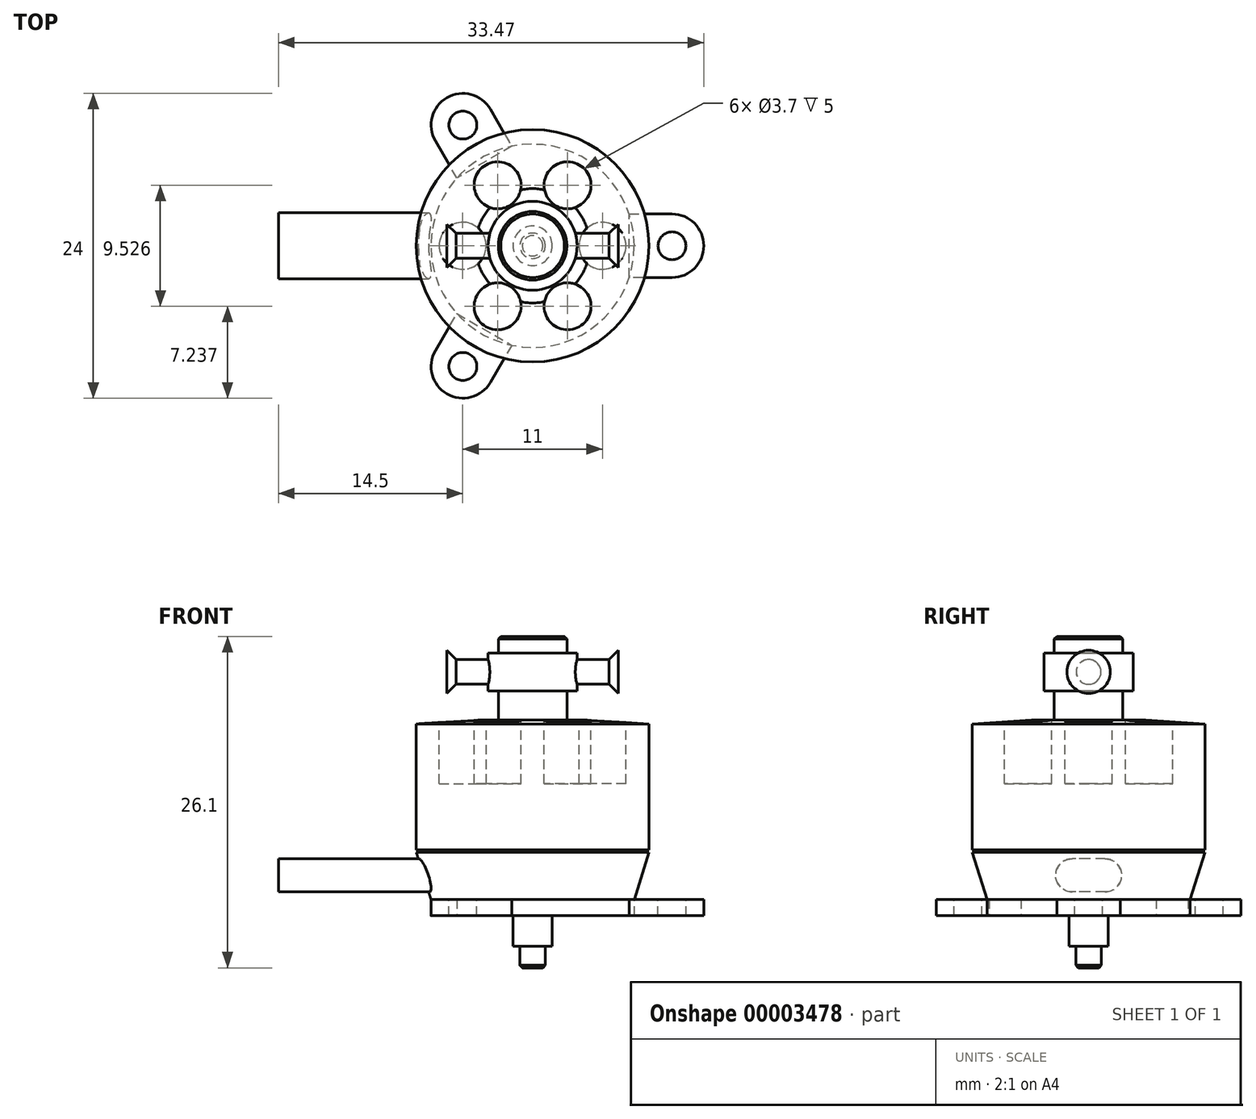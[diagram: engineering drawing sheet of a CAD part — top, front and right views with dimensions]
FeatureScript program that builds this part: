
annotation { "Feature Type Name" : "Feature", "Feature Type Description" : "" }
export const myFeature = defineFeature(function(context is Context, id is Id, definition is map)
    precondition{}
    {
        {
            var Q0;
            Q0=qCreatedBy(makeId("Top.planeOp"),FACE);
            var sketch = newSketch(context, id + "F0", { "sketchPlane" : qUnion([Q0])});
            skCircle(sketch, "E0", {"center": v(0, 0) * mm, "radius": 9.15 * mm});
            skSolve(sketch);
        }
        {
            var Q0;
            Q0=makeQuery(id+"F0.imprint","IMPRINT",FACE,{"disambiguationData":[TD([[makeQuery(id+"F0.imprint","IMPRINT",EDGE,{"derivedFrom":sQuery(id+"F0.wireOp",EDGE,"E0")}),1.0]])]});
            extrude(context, id + "F1", {"entities" : qUnion([Q0]), "depth" : 10.2 * mm});
        }
        {
            var Q0;
            Q0=makeQuery(id+"F1.opExtrude","CAP_FACE",FACE,{"disambiguationData":[OSD([sQuery(id+"F0.wireOp",EDGE,"E0")])],"isStart":true});
            var sketch = newSketch(context, id + "F2", { "sketchPlane" : qUnion([Q0])});
            skCircle(sketch, "E1", {"center": v(0, 0) * mm, "radius": 8 * mm});
            skSolve(sketch);
        }
        {
            var Q0;
            Q0=makeQuery(id+"F2.imprint","IMPRINT",FACE,{"disambiguationData":[TD([[makeQuery(id+"F2.imprint","IMPRINT",EDGE,{"derivedFrom":sQuery(id+"F2.wireOp",EDGE,"E1")}),1.0]])]});
            extrude(context, id + "F3", {"entities" : qUnion([Q0]), "operationType" : NewBodyOperationType.ADD, "depth" : 0.2 * mm});
        }
        {
            var Q0;
            Q0=makeQuery(id+"F3.opExtrude","CAP_FACE",FACE,{"disambiguationData":[OSD([sQuery(id+"F2.wireOp",EDGE,"E1")])],"isStart":false});
            var sketch = newSketch(context, id + "F4", { "sketchPlane" : qUnion([Q0])});
            skCircle(sketch, "E2", {"center": v(0, 0) * mm, "radius": 9.15 * mm});
            skSolve(sketch);
        }
        {
            var Q0;
            {var subQ0=makeQuery(id+"F4.imprint","IMPRINT",EDGE,{"derivedFrom":makeQuery(id+"F3.opExtrude","CAP_EDGE",EDGE,{"disambiguationData":[OSD([sQuery(id+"F2.wireOp",EDGE,"E1")])],"isStart":false})});Q0=qUnion([makeQuery(id+"F4.imprint","IMPRINT",FACE,{"disambiguationData":[TD([[makeQuery(id+"F4.imprint","IMPRINT",EDGE,{"derivedFrom":sQuery(id+"F4.wireOp",EDGE,"E2")}),1.0]])]}),makeQuery(id+"F4.imprint","IMPRINT",FACE,{"disambiguationData":[TD([[subQ0,1.0]])]})]);}
            extrude(context, id + "F5", {"entities" : qUnion([Q0]), "depth" : 3.7 * mm});
        }
        {
            var Q0;
            Q0=makeQuery(id+"F5.opExtrude","CAP_EDGE",EDGE,{"disambiguationData":[OSD([sQuery(id+"F4.wireOp",EDGE,"E2")])],"isStart":false});
            chamfer(context, id + "F6", {"entities" : qUnion([Q0]), "chamferType" : ChamferType.TWO_OFFSETS, "width1" : 1.15 * mm, "oppositeDirection" : false, "width2" : 3.7 * mm, "tangentPropagation" : true});
        }
        {
            var Q0;
            Q0=makeQuery(id+"F5.opExtrude","CAP_FACE",FACE,{"disambiguationData":[OSD([sQuery(id+"F4.wireOp",EDGE,"E2")])],"isStart":false});
            var sketch = newSketch(context, id + "F7", { "sketchPlane" : qUnion([Q0])});
            skCircle(sketch, "E3", {"center": v(0, 0) * mm, "radius": 8 * mm});
            skSolve(sketch);
        }
        {
            var Q0;
            Q0=makeQuery(id+"F7.imprint","IMPRINT",FACE,{"disambiguationData":[TD([[makeQuery(id+"F7.imprint","IMPRINT",EDGE,{"derivedFrom":sQuery(id+"F7.wireOp",EDGE,"E3")}),1.0]])]});
            extrude(context, id + "F8", {"entities" : qUnion([Q0]), "operationType" : NewBodyOperationType.ADD, "depth" : 1.3 * mm});
        }
        {
            var Q0;
            Q0=makeQuery(id+"F8.opExtrude","CAP_FACE",FACE,{"disambiguationData":[OSD([sQuery(id+"F7.wireOp",EDGE,"E3")])],"isStart":false});
            var sketch = newSketch(context, id + "F9", { "sketchPlane" : qUnion([Q0])});
            skLineSegment(sketch, "E4", {"start": v(0, 0) * mm, "end": v(10.97, 0) * mm, "construction": true});
            skLineSegment(sketch, "E5", {"start": v(10.97, 2.5) * mm, "end": v(10.97, -2.5) * mm, "construction": true});
            skArc(sketch, "E6", {"start": v(10.97, -2.5) * mm, "mid": v(13.47, 0) * mm, "end": v(10.97, 2.5) * mm});
            skLineSegment(sketch, "E7", {"start": v(10.97, 2.5) * mm, "end": v(7.6, 2.5) * mm});
            skLineSegment(sketch, "E8", {"start": v(7.6, 2.5) * mm, "end": v(7.6, -2.5) * mm});
            skLineSegment(sketch, "E9", {"start": v(7.6, -2.5) * mm, "end": v(10.97, -2.5) * mm});
            skLineSegment(sketch, "E10", {"start": v(0, 0) * mm, "end": v(-5.48, -9.5) * mm, "construction": true});
            skLineSegment(sketch, "E11", {"start": v(0, 0) * mm, "end": v(-5.48, 9.5) * mm, "construction": true});
            skSolve(sketch);
        }
        {
            var Q0;
            {var subQ1=sQuery(id+"F9.wireOp",EDGE,"E8");Q0=qUnion([makeQuery(id+"F9.imprint","IMPRINT",FACE,{"disambiguationData":[TD([[makeQuery(id+"F9.imprint","IMPRINT",EDGE,{"derivedFrom":sQuery(id+"F9.wireOp",EDGE,"E6")}),1.0]])]}),makeQuery(id+"F9.imprint","IMPRINT",FACE,{"disambiguationData":[TD([[makeQuery(id+"F9.imprint","IMPRINT",EDGE,{"derivedFrom":subQ1}),1.0]])]})]);}
            var Q1;
            Q1=sQuery(id+"F9.wireOp",EDGE,"E6");
            var Q2;
            Q2=makeQuery(id+"F6.opChamfer","BLEND_FACE",FACE,{"disambiguationData":[OSD([sQuery(id+"F4.wireOp",EDGE,"E2")])]});
            extrude(context, id + "F10", {"entities" : qUnion([Q0]), "surfaceEntities" : qUnion([Q1]), "oppositeDirection" : true, "endBoundEntity" : qUnion([Q2]), "depth" : 1.3 * mm});
        }
        {
            var Q0;
            Q0=makeQuery(id+"F10.opExtrude","CAP_FACE",FACE,{"disambiguationData":[OSD([sQuery(id+"F9.wireOp",EDGE,"E6"),sQuery(id+"F9.wireOp",EDGE,"E7"),sQuery(id+"F9.wireOp",EDGE,"E8"),sQuery(id+"F9.wireOp",EDGE,"E9")])],"isStart":false});
            var sketch = newSketch(context, id + "F11", { "sketchPlane" : qUnion([Q0])});
            skCircle(sketch, "E12", {"center": v(10.97, 0) * mm, "radius": 1.1 * mm});
            skSolve(sketch);
        }
        {
            var Q0;
            Q0=makeQuery(id+"F11.imprint","IMPRINT",FACE,{"disambiguationData":[TD([[makeQuery(id+"F11.imprint","IMPRINT",EDGE,{"derivedFrom":sQuery(id+"F11.wireOp",EDGE,"E12")}),1.0]])]});
            extrude(context, id + "F12", {"entities" : qUnion([Q0]), "operationType" : NewBodyOperationType.REMOVE, "endBound" : BoundingType.THROUGH_ALL, "oppositeDirection" : true, "depth" : 25 * mm});
        }
        {
            var Q0;
            Q0=makeQuery(id+"F10.opExtrude","SWEPT_BODY",BODY,{"disambiguationData":[OSD([sQuery(id+"F9.wireOp",EDGE,"E6"),sQuery(id+"F9.wireOp",EDGE,"E7"),sQuery(id+"F9.wireOp",EDGE,"E8"),sQuery(id+"F9.wireOp",EDGE,"E9")])]});
            var Q1;
            Q1=makeQuery(id+"F1.opExtrude","SWEPT_FACE",FACE,{"disambiguationData":[OSD([sQuery(id+"F0.wireOp",EDGE,"E0")])]});
            circularPattern(context, id + "F13", {"entities" : qUnion([Q0]), "axis" : qUnion([Q1]), "angle" : 360 * degree, "instanceCount" : 3, "equalSpace" : true});
        }
        {
            var Q0;
            Q0=qCreatedBy(makeId("Right.planeOp"),FACE);
            var sketch = newSketch(context, id + "F14", { "sketchPlane" : qUnion([Q0])});
            skLineSegment(sketch, "E13", {"start": v(0, 0) * mm, "end": v(0, -8.18) * mm, "construction": true});
            skLineSegment(sketch, "E14", {"start": v(1.3, -0.72) * mm, "end": v(0, -0.72) * mm});
            skLineSegment(sketch, "E15", {"start": v(0, -0.72) * mm, "end": v(-1.3, -0.72) * mm});
            skLineSegment(sketch, "E16", {"start": v(1.3, -3.32) * mm, "end": v(0, -3.32) * mm});
            skLineSegment(sketch, "E17", {"start": v(0, -3.32) * mm, "end": v(-1.3, -3.32) * mm});
            skArc(sketch, "E18", {"start": v(1.3, -0.72) * mm, "mid": v(2.6, -2.02) * mm, "end": v(1.3, -3.32) * mm});
            skArc(sketch, "E19", {"start": v(-1.3, -0.72) * mm, "mid": v(-2.6, -2.02) * mm, "end": v(-1.3, -3.32) * mm});
            skPoint(sketch, "E20", {"position": v(2.6, -2.02) * mm});
            skPoint(sketch, "E21", {"position": v(-2.6, -2.02) * mm});
            skSolve(sketch);
        }
        {
            var Q0;
            Q0 = qSketchRegion(id + "F14", true);
            extrude(context, id + "F15", {"entities" : qUnion([Q0]), "operationType" : NewBodyOperationType.ADD, "oppositeDirection" : true, "depth" : 20 * mm});
        }
        {
            var Q0;
            Q0=makeQuery(id+"F8.opExtrude","CAP_FACE",FACE,{"disambiguationData":[OSD([sQuery(id+"F7.wireOp",EDGE,"E3")])],"isStart":false});
            var sketch = newSketch(context, id + "F16", { "sketchPlane" : qUnion([Q0])});
            skCircle(sketch, "E22", {"center": v(0, 0) * mm, "radius": 1.55 * mm});
            skSolve(sketch);
        }
        {
            var Q0;
            Q0=makeQuery(id+"F16.imprint","IMPRINT",FACE,{"disambiguationData":[TD([[makeQuery(id+"F16.imprint","IMPRINT",EDGE,{"derivedFrom":sQuery(id+"F16.wireOp",EDGE,"E22")}),1.0]])]});
            extrude(context, id + "F17", {"entities" : qUnion([Q0]), "operationType" : NewBodyOperationType.ADD, "depth" : 2.4 * mm});
        }
        {
            var Q0;
            Q0=makeQuery(id+"F17.opExtrude","CAP_FACE",FACE,{"disambiguationData":[OSD([sQuery(id+"F16.wireOp",EDGE,"E22")])],"isStart":false});
            var sketch = newSketch(context, id + "F18", { "sketchPlane" : qUnion([Q0])});
            skCircle(sketch, "E23", {"center": v(0, 0) * mm, "radius": 1 * mm});
            skSolve(sketch);
        }
        {
            var Q0;
            Q0=makeQuery(id+"F18.imprint","IMPRINT",FACE,{"disambiguationData":[TD([[makeQuery(id+"F18.imprint","IMPRINT",EDGE,{"derivedFrom":sQuery(id+"F18.wireOp",EDGE,"E23")}),1.0]])]});
            extrude(context, id + "F19", {"entities" : qUnion([Q0]), "operationType" : NewBodyOperationType.ADD, "depth" : 1.7 * mm});
        }
        {
            var Q0;
            Q0=makeQuery(id+"F19.opExtrude","CAP_EDGE",EDGE,{"disambiguationData":[OSD([sQuery(id+"F18.wireOp",EDGE,"E23")])],"isStart":false});
            chamfer(context, id + "F20", {"entities" : qUnion([Q0]), "width" : 0.2 * mm, "tangentPropagation" : true});
        }
        {
            var Q0;
            Q0=makeQuery(id+"F1.opExtrude","CAP_EDGE",EDGE,{"disambiguationData":[OSD([sQuery(id+"F0.wireOp",EDGE,"E0")])],"isStart":false});
            chamfer(context, id + "F21", {"entities" : qUnion([Q0]), "chamferType" : ChamferType.TWO_OFFSETS, "width1" : 4.65 * mm, "oppositeDirection" : false, "width2" : 0.3 * mm, "tangentPropagation" : true});
        }
        {
            var Q0;
            Q0=makeQuery(id+"F1.opExtrude","CAP_FACE",FACE,{"disambiguationData":[OSD([sQuery(id+"F0.wireOp",EDGE,"E0")])],"isStart":false});
            var sketch = newSketch(context, id + "F22", { "sketchPlane" : qUnion([Q0])});
            skCircle(sketch, "E24", {"center": v(0, 0) * mm, "radius": 2.7 * mm});
            skSolve(sketch);
        }
        {
            var Q0;
            Q0=makeQuery(id+"F22.imprint","IMPRINT",FACE,{"disambiguationData":[TD([[makeQuery(id+"F22.imprint","IMPRINT",EDGE,{"derivedFrom":sQuery(id+"F22.wireOp",EDGE,"E24")}),1.0]])]});
            extrude(context, id + "F23", {"entities" : qUnion([Q0]), "operationType" : NewBodyOperationType.ADD, "depth" : 2.3 * mm});
        }
        {
            var Q0;
            Q0=makeQuery(id+"F23.opExtrude","CAP_FACE",FACE,{"disambiguationData":[OSD([sQuery(id+"F22.wireOp",EDGE,"E24")])],"isStart":false});
            var sketch = newSketch(context, id + "F24", { "sketchPlane" : qUnion([Q0])});
            skCircle(sketch, "E25", {"center": v(0, 0) * mm, "radius": 3.5 * mm});
            skSolve(sketch);
        }
        {
            var Q0;
            {var subQ0=makeQuery(id+"F24.imprint","IMPRINT",EDGE,{"derivedFrom":makeQuery(id+"F23.opExtrude","CAP_EDGE",EDGE,{"disambiguationData":[OSD([sQuery(id+"F22.wireOp",EDGE,"E24")])],"isStart":false})});Q0=qUnion([makeQuery(id+"F24.imprint","IMPRINT",FACE,{"disambiguationData":[TD([[makeQuery(id+"F24.imprint","IMPRINT",EDGE,{"derivedFrom":sQuery(id+"F24.wireOp",EDGE,"E25")}),1.0]])]}),makeQuery(id+"F24.imprint","IMPRINT",FACE,{"disambiguationData":[TD([[subQ0,1.0]])]})]);}
            extrude(context, id + "F25", {"entities" : qUnion([Q0]), "operationType" : NewBodyOperationType.ADD, "depth" : 3 * mm});
        }
        {
            var Q0;
            Q0=makeQuery(id+"F25.opExtrude","CAP_FACE",FACE,{"disambiguationData":[OSD([sQuery(id+"F24.wireOp",EDGE,"E25")])],"isStart":false});
            var sketch = newSketch(context, id + "F26", { "sketchPlane" : qUnion([Q0])});
            skCircle(sketch, "E26", {"center": v(0, 0) * mm, "radius": 2.7 * mm});
            skSolve(sketch);
        }
        {
            var Q0;
            Q0=makeQuery(id+"F26.imprint","IMPRINT",FACE,{"disambiguationData":[TD([[makeQuery(id+"F26.imprint","IMPRINT",EDGE,{"derivedFrom":sQuery(id+"F26.wireOp",EDGE,"E26")}),1.0]])]});
            extrude(context, id + "F27", {"entities" : qUnion([Q0]), "operationType" : NewBodyOperationType.ADD, "depth" : 1.3 * mm});
        }
        {
            var Q0;
            Q0=makeQuery(id+"F27.opExtrude","CAP_EDGE",EDGE,{"disambiguationData":[OSD([sQuery(id+"F26.wireOp",EDGE,"E26")])],"isStart":false});
            chamfer(context, id + "F28", {"entities" : qUnion([Q0]), "width" : 0.2 * mm, "tangentPropagation" : true});
        }
        {
            var Q0;
            Q0=makeQuery(id+"F1.opExtrude","CAP_FACE",FACE,{"disambiguationData":[OSD([sQuery(id+"F0.wireOp",EDGE,"E0")])],"isStart":false});
            var sketch = newSketch(context, id + "F29", { "sketchPlane" : qUnion([Q0])});
            skCircle(sketch, "E27", {"center": v(5.5, 0) * mm, "radius": 1.85 * mm});
            skLineSegment(sketch, "E28", {"start": v(0, 0) * mm, "end": v(5.5, 0) * mm, "construction": true});
            skSolve(sketch);
        }
        {
            var Q0;
            {var subQ0=sQuery(id+"F0.wireOp",EDGE,"E0");var subQ1=makeQuery(id+"F21.opChamfer","BLEND_EDGE",EDGE,{"blendedFrom":[makeQuery(id+"F1.opExtrude","CAP_EDGE",EDGE,{"disambiguationData":[OSD([subQ0])],"isStart":false}),makeQuery(id+"F1.opExtrude","CAP_FACE",FACE,{"disambiguationData":[OSD([subQ0])],"isStart":false})],"blendedInto":[makeQuery(id+"F1.opExtrude","CAP_FACE",FACE,{"disambiguationData":[OSD([subQ0])],"isStart":false})]});var subQ2=sQuery(id+"F29.wireOp",EDGE,"E27");var subQ4=makeQuery(id+"F29.imprint","INTERSECT",VERTEX,{"disambiguationData":[OD(0.0)],"derivedFrom":[subQ1,subQ2]});Q0=qUnion([makeQuery(id+"F29.imprint","IMPRINT",FACE,{"disambiguationData":[TD([[makeQuery(id+"F29.imprint","IMPRINT",EDGE,{"disambiguationData":[TD([[subQ4,-1.0]])],"derivedFrom":subQ2}),1.0]])]}),makeQuery(id+"F29.imprint","IMPRINT",FACE,{"disambiguationData":[TD([[makeQuery(id+"F29.imprint","IMPRINT",EDGE,{"disambiguationData":[TD([[subQ4,1.0]])],"derivedFrom":subQ2}),1.0]])]})]);}
            extrude(context, id + "F30", {"entities" : qUnion([Q0]), "operationType" : NewBodyOperationType.REMOVE, "oppositeDirection" : true, "depth" : 5 * mm});
        }
        {
            var Q0;
            Q0=makeQuery(id+"F30.boolean.opBoolean","COPY",FACE,{"derivedFrom":makeQuery(id+"F30.opExtrude","SWEPT_FACE",FACE,{"disambiguationData":[OSD([sQuery(id+"F29.wireOp",EDGE,"E27")])]})});
            var Q1;
            Q1=makeQuery(id+"F30.boolean.opBoolean","COPY",FACE,{"derivedFrom":makeQuery(id+"F30.opExtrude","CAP_FACE",FACE,{"disambiguationData":[OSD([sQuery(id+"F29.wireOp",EDGE,"E27")])],"isStart":false})});
            var Q2;
            Q2=makeQuery(id+"F1.opExtrude","SWEPT_FACE",FACE,{"disambiguationData":[OSD([sQuery(id+"F0.wireOp",EDGE,"E0")])]});
            circularPattern(context, id + "F31", {"faces" : qUnion([Q0, Q1]), "axis" : qUnion([Q2]), "angle" : 360 * degree, "instanceCount" : 6, "equalSpace" : true, "patternType" : PatternType.FACE});
        }
        {
            var Q0;
            Q0=qCreatedBy(makeId("Right.planeOp"),FACE);
            var sketch = newSketch(context, id + "F32", { "sketchPlane" : qUnion([Q0])});
            skLineSegment(sketch, "E29", {"start": v(0, 15.5) * mm, "end": v(0, 12.5) * mm, "construction": true});
            skCircle(sketch, "E30", {"center": v(0, 14) * mm, "radius": 0.97 * mm});
            skSolve(sketch);
        }
        {
            var Q0;
            Q0=makeQuery(id+"F32.imprint","IMPRINT",FACE,{"disambiguationData":[TD([[makeQuery(id+"F32.imprint","IMPRINT",EDGE,{"derivedFrom":sQuery(id+"F32.wireOp",EDGE,"E30")}),1.0]])]});
            extrude(context, id + "F33", {"entities" : qUnion([Q0]), "operationType" : NewBodyOperationType.ADD, "depth" : 5.75 * mm});
        }
        {
            var Q0;
            Q0=makeQuery(id+"F33.opExtrude","CAP_FACE",FACE,{"disambiguationData":[OSD([sQuery(id+"F32.wireOp",EDGE,"E30")])],"isStart":false});
            var sketch = newSketch(context, id + "F34", { "sketchPlane" : qUnion([Q0])});
            skCircle(sketch, "E31", {"center": v(0, 14) * mm, "radius": 1.7 * mm});
            skSolve(sketch);
        }
        {
            var Q0;
            {var subQ0=makeQuery(id+"F34.imprint","IMPRINT",EDGE,{"derivedFrom":makeQuery(id+"F33.opExtrude","CAP_EDGE",EDGE,{"disambiguationData":[OSD([sQuery(id+"F32.wireOp",EDGE,"E30")])],"isStart":false})});Q0=qUnion([makeQuery(id+"F34.imprint","IMPRINT",FACE,{"disambiguationData":[TD([[makeQuery(id+"F34.imprint","IMPRINT",EDGE,{"derivedFrom":sQuery(id+"F34.wireOp",EDGE,"E31")}),1.0]])]}),makeQuery(id+"F34.imprint","IMPRINT",FACE,{"disambiguationData":[TD([[subQ0,1.0]])]})]);}
            extrude(context, id + "F35", {"entities" : qUnion([Q0]), "operationType" : NewBodyOperationType.ADD, "depth" : 1 * mm});
        }
        {
            var Q0;
            Q0=makeQuery(id+"F35.opExtrude","CAP_EDGE",EDGE,{"disambiguationData":[OSD([sQuery(id+"F34.wireOp",EDGE,"E31")])],"isStart":true});
            chamfer(context, id + "F36", {"entities" : qUnion([Q0]), "width" : 1 * mm, "tangentPropagation" : true});
        }
        {
            var Q0;
            Q0=makeQuery(id+"F35.opExtrude","CAP_FACE",FACE,{"disambiguationData":[OSD([sQuery(id+"F34.wireOp",EDGE,"E31")])],"isStart":false});
            var Q1;
            Q1=makeQuery(id+"F33.opExtrude","SWEPT_FACE",FACE,{"disambiguationData":[OSD([sQuery(id+"F32.wireOp",EDGE,"E30")])]});
            var Q2;
            Q2=makeQuery(id+"F36.opChamfer","BLEND_FACE",FACE,{"disambiguationData":[OSD([sQuery(id+"F34.wireOp",EDGE,"E31")])]});
            var Q3;
            Q3=qCreatedBy(makeId("Right.planeOp"),FACE);
            mirror(context, id + "F37", {"faces" : qUnion([Q0, Q1, Q2]), "mirrorPlane" : qUnion([Q3]), "patternType" : MirrorType.FACE});
        }
    });
